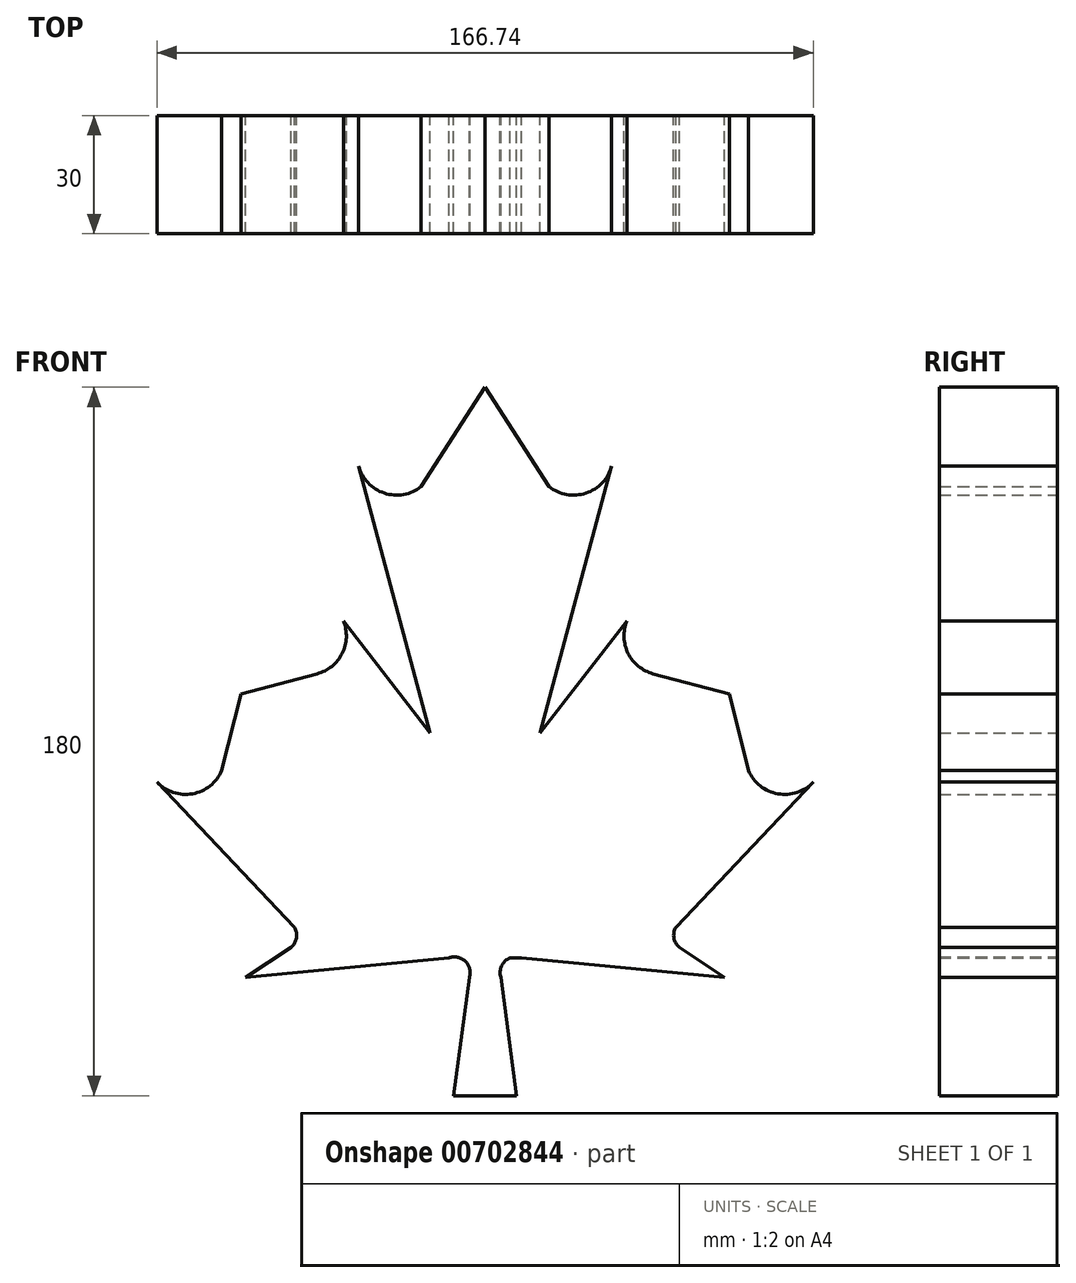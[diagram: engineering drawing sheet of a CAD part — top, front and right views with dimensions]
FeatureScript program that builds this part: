
annotation { "Feature Type Name" : "Feature", "Feature Type Description" : "" }
export const myFeature = defineFeature(function(context is Context, id is Id, definition is map)
    precondition{}
    {
        {
            var Q0;
            Q0=qCreatedBy(makeId("Front.planeOp"),FACE);
            var sketch = newSketch(context, id + "F0", { "sketchPlane" : qUnion([Q0])});
            skLineSegment(sketch, "E0", {"start": v(0, 98.66) * mm, "end": v(0, -81.34) * mm});
            skLineSegment(sketch, "E1", {"start": v(0, -51.34) * mm, "end": v(4, -51.34) * mm});
            skLineSegment(sketch, "E2", {"start": v(13.99, 10.86) * mm, "end": v(32.15, 78.66) * mm});
            skLineSegment(sketch, "E3", {"start": v(0, 98.66) * mm, "end": v(16.25, 73.44) * mm});
            skArc(sketch, "E4", {"start": v(16.25, 73.44) * mm, "mid": v(25.61, 71.74) * mm, "end": v(32.15, 78.66) * mm});
            skLineSegment(sketch, "E5", {"start": v(-36.74, -81.34) * mm, "end": v(37.77, -81.34) * mm});
            skLineSegment(sketch, "E6", {"start": v(8, -81.34) * mm, "end": v(4, -51.34) * mm});
            skLineSegment(sketch, "E7", {"start": v(6.37, -46.34) * mm, "end": v(9.22, -46.34) * mm});
            skArc(sketch, "E8", {"start": v(9.22, -46.34) * mm, "mid": v(5.03, -47.2) * mm, "end": v(4, -51.34) * mm});
            skLineSegment(sketch, "E9", {"start": v(9.22, -46.34) * mm, "end": v(60.85, -51.34) * mm});
            skLineSegment(sketch, "E10", {"start": v(62, 20.66) * mm, "end": v(66.91, 1.27) * mm});
            skLineSegment(sketch, "E11", {"start": v(62, 20.66) * mm, "end": v(42.68, 25.83) * mm});
            skArc(sketch, "E12", {"start": v(66.91, 1.27) * mm, "mid": v(74.35, -4.64) * mm, "end": v(83.37, -1.66) * mm});
            skLineSegment(sketch, "E13", {"start": v(13.99, 10.86) * mm, "end": v(36, 39.25) * mm});
            skArc(sketch, "E14", {"start": v(36, 39.25) * mm, "mid": v(36.32, 31.04) * mm, "end": v(42.68, 25.83) * mm});
            skLineSegment(sketch, "E15.trimOffspring", {"start": v(48.44, -38.59) * mm, "end": v(83.37, -1.66) * mm});
            skLineSegment(sketch, "E16", {"start": v(60.85, -51.34) * mm, "end": v(49.33, -43.67) * mm});
            skArc(sketch, "E17", {"start": v(49.7, -37.26) * mm, "mid": v(47.9, -40.38) * mm, "end": v(49.33, -43.67) * mm});
            skLineSegment(sketch, "E18.MirrorCS", {"start": v(-9.22, -46.34) * mm, "end": v(-60.85, -51.34) * mm});
            skLineSegment(sketch, "E19.MirrorCS", {"start": v(-8, -81.34) * mm, "end": v(-4, -51.34) * mm});
            skArc(sketch, "E20.MirrorCS", {"start": v(-9.22, -46.34) * mm, "mid": v(-5.03, -47.2) * mm, "end": v(-4, -51.34) * mm});
            skLineSegment(sketch, "E21.MirrorCS", {"start": v(-60.85, -51.34) * mm, "end": v(-49.33, -43.67) * mm});
            skArc(sketch, "E22.MirrorCS", {"start": v(-49.7, -37.26) * mm, "mid": v(-47.9, -40.38) * mm, "end": v(-49.33, -43.67) * mm});
            skLineSegment(sketch, "E23.MirrorCS", {"start": v(-48.44, -38.59) * mm, "end": v(-83.37, -1.66) * mm});
            skArc(sketch, "E24.MirrorCS", {"start": v(-66.91, 1.27) * mm, "mid": v(-74.35, -4.64) * mm, "end": v(-83.37, -1.66) * mm});
            skLineSegment(sketch, "E25.MirrorCS", {"start": v(-62, 20.66) * mm, "end": v(-66.91, 1.27) * mm});
            skLineSegment(sketch, "E26.MirrorCS", {"start": v(-62, 20.66) * mm, "end": v(-42.68, 25.83) * mm});
            skArc(sketch, "E27.MirrorCS", {"start": v(-36, 39.25) * mm, "mid": v(-36.32, 31.04) * mm, "end": v(-42.68, 25.83) * mm});
            skLineSegment(sketch, "E28.MirrorCS", {"start": v(-13.99, 10.86) * mm, "end": v(-36, 39.25) * mm});
            skLineSegment(sketch, "E29.MirrorCS", {"start": v(-13.99, 10.86) * mm, "end": v(-32.15, 78.66) * mm});
            skArc(sketch, "E30.MirrorCS", {"start": v(-16.25, 73.44) * mm, "mid": v(-25.61, 71.74) * mm, "end": v(-32.15, 78.66) * mm});
            skLineSegment(sketch, "E31.MirrorCS", {"start": v(0, 98.66) * mm, "end": v(-16.25, 73.44) * mm});
            skSolve(sketch);
        }
        {
            var Q0;
            Q0 = qSketchRegion(id + "F0", true);
            var Q1;
            {var subQ4=sQuery(id+"F0.wireOp",EDGE,"E1");Q1=makeQuery(id+"F0.imprint","IMPRINT",FACE,{"disambiguationData":[TD([[makeQuery(id+"F0.imprint","IMPRINT",EDGE,{"derivedFrom":subQ4}),1.0]])]});}
            extrude(context, id + "F1", {"entities" : qUnion([Q0, Q1]), "depth" : 30 * mm, "offsetDistance" : 25 * mm});
        }
    });
